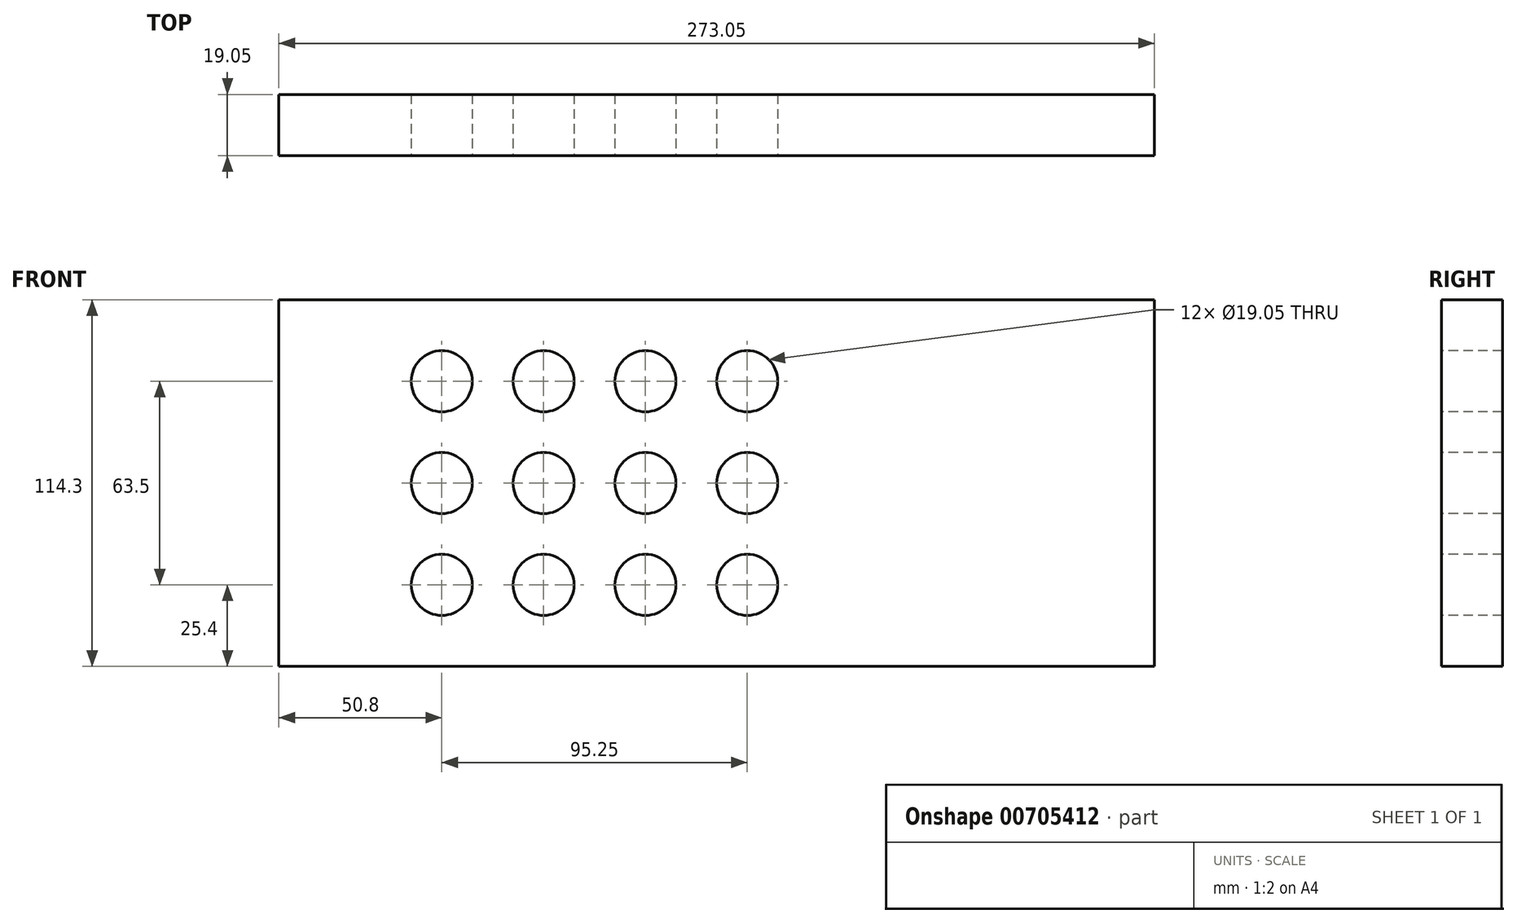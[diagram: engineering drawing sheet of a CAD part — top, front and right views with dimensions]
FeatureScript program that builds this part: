
annotation { "Feature Type Name" : "Feature", "Feature Type Description" : "" }
export const myFeature = defineFeature(function(context is Context, id is Id, definition is map)
    precondition{}
    {
        {
            var Q0;
            Q0=qCreatedBy(makeId("Front.planeOp"),FACE);
            var sketch = newSketch(context, id + "F0", { "sketchPlane" : qUnion([Q0])});
            skLineSegment(sketch, "E0.bottom", {"start": v(0, 0) * mm, "end": v(273.05, 0) * mm});
            skLineSegment(sketch, "E0.top", {"start": v(0, 114.3) * mm, "end": v(273.05, 114.3) * mm});
            skLineSegment(sketch, "E0.left", {"start": v(0, 0) * mm, "end": v(0, 114.3) * mm});
            skLineSegment(sketch, "E0.right", {"start": v(273.05, 0) * mm, "end": v(273.05, 114.3) * mm});
            skSolve(sketch);
        }
        {
            var Q0;
            Q0 = qSketchRegion(id + "F0", true);
            extrude(context, id + "F1", {"entities" : qUnion([Q0]), "depth" : 19.05 * mm, "offsetDistance" : 25.4 * mm});
        }
        {
            var Q0;
            Q0=makeQuery(id+"F1.opExtrude","CAP_FACE",FACE,{"disambiguationData":[OSD([sQuery(id+"F0.wireOp",EDGE,"E0.bottom"),sQuery(id+"F0.wireOp",EDGE,"E0.top"),sQuery(id+"F0.wireOp",EDGE,"E0.left"),sQuery(id+"F0.wireOp",EDGE,"E0.right")])],"isStart":false});
            var sketch = newSketch(context, id + "F2", { "sketchPlane" : qUnion([Q0])});
            skCircle(sketch, "E1", {"center": v(50.8, 88.9) * mm, "radius": 9.53 * mm});
            skCircle(sketch, "E2", {"center": v(50.8, 57.15) * mm, "radius": 9.53 * mm});
            skCircle(sketch, "E3", {"center": v(82.55, 88.9) * mm, "radius": 9.53 * mm});
            skCircle(sketch, "E4", {"center": v(82.55, 57.15) * mm, "radius": 9.53 * mm});
            skCircle(sketch, "E5", {"center": v(114.3, 88.9) * mm, "radius": 9.53 * mm});
            skCircle(sketch, "E6", {"center": v(114.3, 57.15) * mm, "radius": 9.53 * mm});
            skCircle(sketch, "E7", {"center": v(50.8, 25.4) * mm, "radius": 9.53 * mm});
            skCircle(sketch, "E8", {"center": v(82.55, 25.4) * mm, "radius": 9.53 * mm});
            skCircle(sketch, "E9", {"center": v(114.3, 25.4) * mm, "radius": 9.53 * mm});
            skCircle(sketch, "E10", {"center": v(146.05, 88.9) * mm, "radius": 9.53 * mm});
            skCircle(sketch, "E11", {"center": v(146.05, 57.15) * mm, "radius": 9.53 * mm});
            skCircle(sketch, "E12", {"center": v(146.05, 25.4) * mm, "radius": 9.53 * mm});
            skSolve(sketch);
        }
        {
            var Q0;
            Q0 = qSketchRegion(id + "F2", true);
            extrude(context, id + "F3", {"entities" : qUnion([Q0]), "operationType" : NewBodyOperationType.REMOVE, "oppositeDirection" : true, "depth" : 25.4 * mm, "offsetDistance" : 25.4 * mm});
        }
    });
